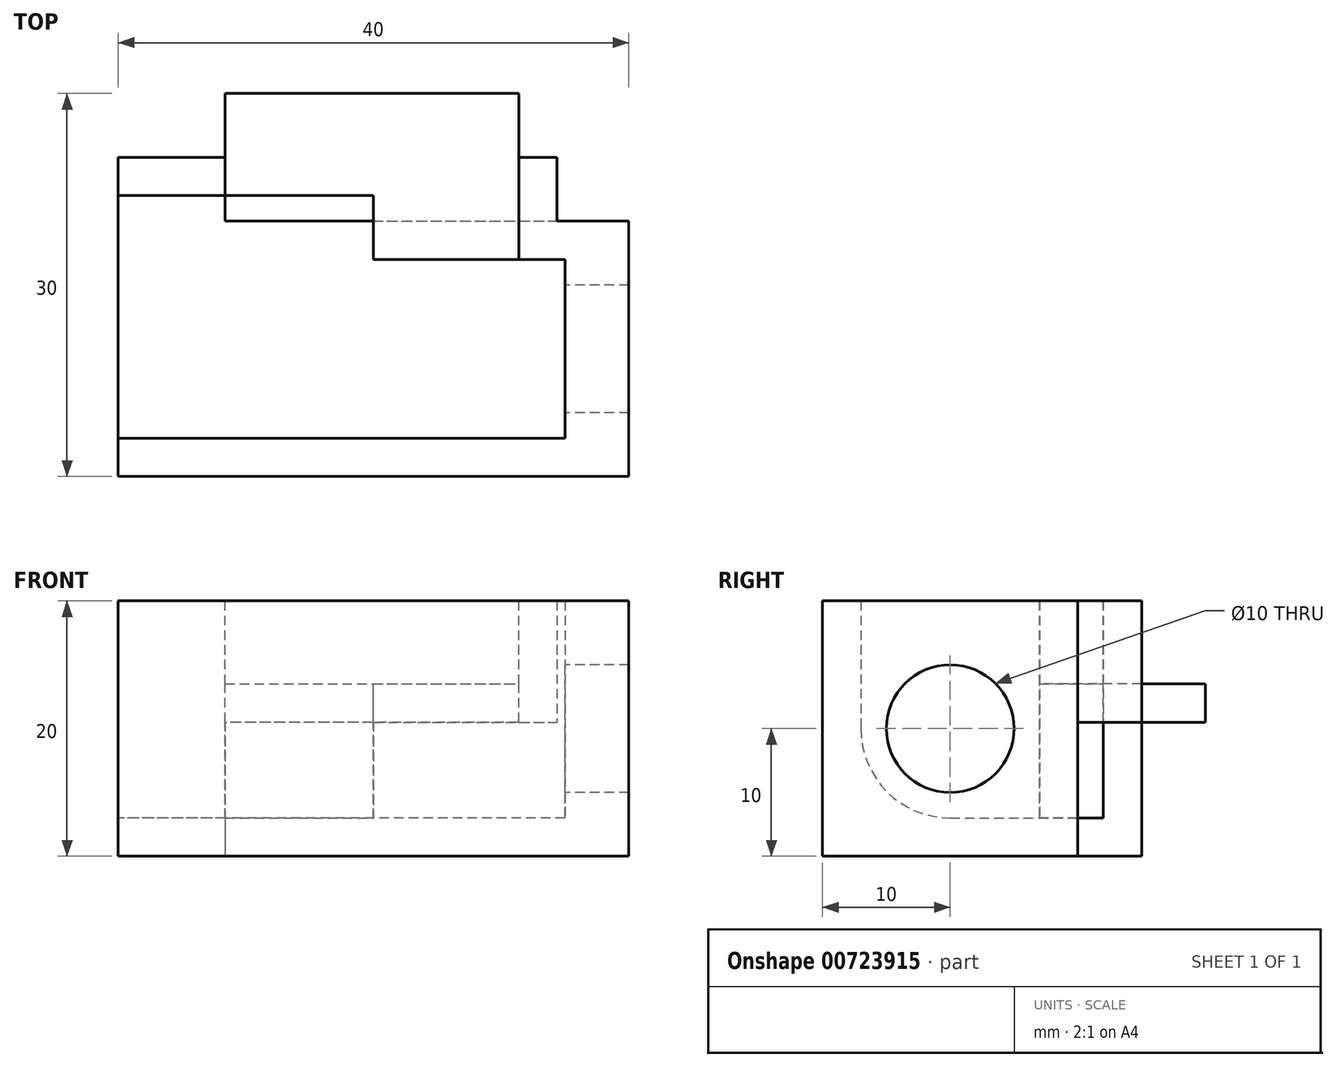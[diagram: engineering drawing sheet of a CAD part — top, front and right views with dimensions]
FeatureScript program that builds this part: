
annotation { "Feature Type Name" : "Feature", "Feature Type Description" : "" }
export const myFeature = defineFeature(function(context is Context, id is Id, definition is map)
    precondition{}
    {
        {
            var Q0;
            Q0=qCreatedBy(makeId("Top.planeOp"),FACE);
            var sketch = newSketch(context, id + "F0", { "sketchPlane" : qUnion([Q0])});
            skLineSegment(sketch, "E0.bottom", {"start": v(-20, 10) * mm, "end": v(20, 10) * mm});
            skLineSegment(sketch, "E0.top", {"start": v(-20, -10) * mm, "end": v(20, -10) * mm});
            skLineSegment(sketch, "E0.left", {"start": v(-20, 10) * mm, "end": v(-20, -10) * mm});
            skLineSegment(sketch, "E0.right", {"start": v(20, 10) * mm, "end": v(20, -10) * mm});
            skPoint(sketch, "E0.middle", {"position": v(0, 0) * mm});
            skSolve(sketch);
        }
        {
            var Q0;
            Q0 = qSketchRegion(id + "F0", true);
            extrude(context, id + "F1", {"entities" : qUnion([Q0]), "depth" : 10 * mm, "offsetDistance" : 25 * mm});
        }
        {
            var Q0;
            Q0=makeQuery(id+"F1.opExtrude","SWEPT_FACE",FACE,{"disambiguationData":[OSD([sQuery(id+"F0.wireOp",EDGE,"E0.left")])]});
            var sketch = newSketch(context, id + "F2", { "sketchPlane" : qUnion([Q0])});
            skLineSegment(sketch, "E1", {"start": v(0, 10) * mm, "end": v(0, 3) * mm, "construction": true});
            skCircle(sketch, "E2", {"center": v(0, 10) * mm, "radius": 7 * mm});
            skCircle(sketch, "E3", {"center": v(0, 10) * mm, "radius": 5 * mm});
            skLineSegment(sketch, "E4.bottom", {"start": v(0, 10) * mm, "end": v(-7, 10) * mm});
            skLineSegment(sketch, "E4.top", {"start": v(0, 3) * mm, "end": v(-7, 3) * mm});
            skLineSegment(sketch, "E4.left", {"start": v(0, 10) * mm, "end": v(0, 3) * mm});
            skLineSegment(sketch, "E4.right", {"start": v(-7, 10) * mm, "end": v(-7, 3) * mm});
            skSolve(sketch);
        }
        {
            var Q0;
            Q0=makeQuery(id+"F1.opExtrude","CAP_FACE",FACE,{"disambiguationData":[OSD([sQuery(id+"F0.wireOp",EDGE,"E0.bottom"),sQuery(id+"F0.wireOp",EDGE,"E0.top"),sQuery(id+"F0.wireOp",EDGE,"E0.left"),sQuery(id+"F0.wireOp",EDGE,"E0.right")])],"isStart":false});
            var sketch = newSketch(context, id + "F3", { "sketchPlane" : qUnion([Q0])});
            skLineSegment(sketch, "E5.bottom", {"start": v(20, 10) * mm, "end": v(15, 10) * mm});
            skLineSegment(sketch, "E5.top", {"start": v(20, -10) * mm, "end": v(15, -10) * mm});
            skLineSegment(sketch, "E5.left", {"start": v(20, 10) * mm, "end": v(20, -10) * mm});
            skLineSegment(sketch, "E5.right", {"start": v(15, 10) * mm, "end": v(15, -10) * mm});
            skLineSegment(sketch, "E6.bottom", {"start": v(-20, 10) * mm, "end": v(15, 10) * mm});
            skLineSegment(sketch, "E6.top", {"start": v(-20, 7) * mm, "end": v(15, 7) * mm});
            skLineSegment(sketch, "E6.left", {"start": v(-20, 10) * mm, "end": v(-20, 7) * mm});
            skLineSegment(sketch, "E6.right", {"start": v(15, 10) * mm, "end": v(15, 7) * mm});
            skLineSegment(sketch, "E7.bottom", {"start": v(-20, -10) * mm, "end": v(15, -10) * mm});
            skLineSegment(sketch, "E7.top", {"start": v(-20, -7) * mm, "end": v(15, -7) * mm});
            skLineSegment(sketch, "E7.left", {"start": v(-20, -10) * mm, "end": v(-20, -7) * mm});
            skLineSegment(sketch, "E7.right", {"start": v(15, -10) * mm, "end": v(15, -7) * mm});
            skSolve(sketch);
        }
        {
            var Q0;
            Q0 = qSketchRegion(id + "F3", true);
            extrude(context, id + "F4", {"entities" : qUnion([Q0]), "operationType" : NewBodyOperationType.ADD, "depth" : 10 * mm, "offsetDistance" : 25 * mm});
        }
        {
            var Q0;
            Q0=makeQuery(id+"F4.opExtrude","CAP_FACE",FACE,{"disambiguationData":[OSD([sQuery(id+"F3.wireOp",EDGE,"E5.bottom"),sQuery(id+"F3.wireOp",EDGE,"E5.top"),sQuery(id+"F3.wireOp",EDGE,"E5.left"),sQuery(id+"F3.wireOp",EDGE,"E5.right"),sQuery(id+"F3.wireOp",EDGE,"E6.bottom"),sQuery(id+"F3.wireOp",EDGE,"E6.top"),sQuery(id+"F3.wireOp",EDGE,"E6.left"),sQuery(id+"F3.wireOp",EDGE,"E7.bottom"),sQuery(id+"F3.wireOp",EDGE,"E7.top"),sQuery(id+"F3.wireOp",EDGE,"E7.left")])],"isStart":false});
            var sketch = newSketch(context, id + "F5", { "sketchPlane" : qUnion([Q0])});
            skLineSegment(sketch, "E8.bottom", {"start": v(11.37, 10) * mm, "end": v(-11.63, 10) * mm});
            skLineSegment(sketch, "E8.top", {"start": v(11.37, 7) * mm, "end": v(-11.63, 7) * mm});
            skLineSegment(sketch, "E8.left", {"start": v(11.37, 10) * mm, "end": v(11.37, 7) * mm});
            skLineSegment(sketch, "E8.right", {"start": v(-11.63, 10) * mm, "end": v(-11.63, 7) * mm});
            skSolve(sketch);
        }
        {
            var Q0;
            Q0=makeQuery(id+"F5.imprint","IMPRINT",FACE,{"disambiguationData":[TD([[makeQuery(id+"F5.imprint","IMPRINT",EDGE,{"derivedFrom":sQuery(id+"F5.wireOp",EDGE,"E8.bottom")}),-1.0]])]});
            extrude(context, id + "F6", {"entities" : qUnion([Q0]), "operationType" : NewBodyOperationType.REMOVE, "oppositeDirection" : true, "depth" : 6.5 * mm, "offsetDistance" : 25 * mm});
        }
        {
            var Q0;
            Q0=makeQuery(id+"F4.boolean.opBoolean","MERGE",FACE,{"derivedFrom":[makeQuery(id+"F1.opExtrude","SWEPT_FACE",FACE,{"disambiguationData":[OSD([sQuery(id+"F0.wireOp",EDGE,"E0.bottom")])]}),makeQuery(id+"F4.opExtrude","SWEPT_FACE",FACE,{"disambiguationData":[OSD([sQuery(id+"F3.wireOp",EDGE,"E5.bottom"),sQuery(id+"F3.wireOp",EDGE,"E6.bottom")])]})]});
            var sketch = newSketch(context, id + "F7", { "sketchPlane" : qUnion([Q0])});
            skLineSegment(sketch, "E9.bottom", {"start": v(-11.37, 13.5) * mm, "end": v(11.63, 13.5) * mm});
            skLineSegment(sketch, "E9.top", {"start": v(-11.37, 10.5) * mm, "end": v(11.63, 10.5) * mm});
            skLineSegment(sketch, "E9.left", {"start": v(-11.37, 13.5) * mm, "end": v(-11.37, 10.5) * mm});
            skLineSegment(sketch, "E9.right", {"start": v(11.63, 13.5) * mm, "end": v(11.63, 10.5) * mm});
            skLineSegment(sketch, "E10.bottom", {"start": v(-11.37, 20) * mm, "end": v(-14.37, 20) * mm});
            skLineSegment(sketch, "E10.top", {"start": v(-11.37, 10.5) * mm, "end": v(-14.37, 10.5) * mm});
            skLineSegment(sketch, "E10.left", {"start": v(-11.37, 20) * mm, "end": v(-11.37, 10.5) * mm});
            skLineSegment(sketch, "E10.right", {"start": v(-14.37, 20) * mm, "end": v(-14.37, 10.5) * mm});
            skLineSegment(sketch, "E11.bottom", {"start": v(20, 20) * mm, "end": v(11.63, 20) * mm});
            skLineSegment(sketch, "E11.top", {"start": v(20, 0) * mm, "end": v(11.63, 0) * mm});
            skLineSegment(sketch, "E11.left", {"start": v(20, 20) * mm, "end": v(20, 0) * mm});
            skLineSegment(sketch, "E11.right", {"start": v(11.63, 20) * mm, "end": v(11.63, 0) * mm});
            skSolve(sketch);
        }
        {
            var Q0;
            Q0 = qSketchRegion(id + "F7", true);
            extrude(context, id + "F8", {"entities" : qUnion([Q0]), "operationType" : NewBodyOperationType.ADD, "depth" : 5 * mm, "offsetDistance" : 25 * mm});
        }
        {
            var Q0;
            {var subQ0=sQuery(id+"F7.wireOp",EDGE,"E9.bottom");Q0=makeQuery(id+"F7.imprint","IMPRINT",FACE,{"disambiguationData":[TD([[makeQuery(id+"F7.imprint","IMPRINT",EDGE,{"derivedFrom":subQ0}),1.0]])]});}
            extrude(context, id + "F9", {"entities" : qUnion([Q0]), "operationType" : NewBodyOperationType.ADD, "depth" : 10 * mm, "offsetDistance" : 25 * mm});
        }
        {
            var Q0;
            {var subQ0=sQuery(id+"F2.wireOp",EDGE,"E2");var subQ1=makeQuery(id+"F1.opExtrude","CAP_EDGE",EDGE,{"disambiguationData":[OSD([sQuery(id+"F0.wireOp",EDGE,"E0.left")])],"isStart":false});var subQ2=makeQuery(id+"F2.imprint","INTERSECT",VERTEX,{"disambiguationData":[OD(0.0)],"derivedFrom":[subQ1,subQ0]});Q0=makeQuery(id+"F2.imprint","IMPRINT",FACE,{"disambiguationData":[TD([[makeQuery(id+"F2.imprint","IMPRINT",EDGE,{"disambiguationData":[TD([[subQ2,-1.0]])],"derivedFrom":subQ0}),1.0]])]});}
            extrude(context, id + "F10", {"entities" : qUnion([Q0]), "operationType" : NewBodyOperationType.REMOVE, "oppositeDirection" : true, "depth" : 35 * mm, "offsetDistance" : 25 * mm});
        }
        {
            var Q0;
            {var subQ0=sQuery(id+"F2.wireOp",EDGE,"E3");var subQ1=makeQuery(id+"F1.opExtrude","CAP_EDGE",EDGE,{"disambiguationData":[OSD([sQuery(id+"F0.wireOp",EDGE,"E0.left")])],"isStart":false});var subQ2=makeQuery(id+"F2.imprint","INTERSECT",VERTEX,{"disambiguationData":[OD(0.0)],"derivedFrom":[subQ1,subQ0]});Q0=makeQuery(id+"F2.imprint","IMPRINT",FACE,{"disambiguationData":[TD([[makeQuery(id+"F2.imprint","IMPRINT",EDGE,{"disambiguationData":[TD([[subQ2,-1.0]])],"derivedFrom":subQ0}),1.0]])]});}
            var Q1;
            {var subQ0=sQuery(id+"F2.wireOp",EDGE,"E3");var subQ1=makeQuery(id+"F1.opExtrude","CAP_EDGE",EDGE,{"disambiguationData":[OSD([sQuery(id+"F0.wireOp",EDGE,"E0.left")])],"isStart":false});var subQ2=makeQuery(id+"F2.imprint","INTERSECT",VERTEX,{"disambiguationData":[OD(0.0)],"derivedFrom":[subQ1,subQ0]});Q1=makeQuery(id+"F2.imprint","IMPRINT",FACE,{"disambiguationData":[TD([[makeQuery(id+"F2.imprint","IMPRINT",EDGE,{"disambiguationData":[TD([[subQ2,1.0]])],"derivedFrom":subQ0}),1.0]])]});}
            extrude(context, id + "F11", {"entities" : qUnion([Q0, Q1]), "operationType" : NewBodyOperationType.REMOVE, "oppositeDirection" : true, "depth" : 40 * mm, "offsetDistance" : 25 * mm});
        }
        {
            var Q0;
            {var subQ0=sQuery(id+"F2.wireOp",EDGE,"E4.bottom");var subQ1=sQuery(id+"F2.wireOp",EDGE,"E3");var subQ2=makeQuery(id+"F2.imprint","INTERSECT",VERTEX,{"derivedFrom":[subQ1,subQ0]});Q0=makeQuery(id+"F2.imprint","IMPRINT",FACE,{"disambiguationData":[TD([[makeQuery(id+"F2.imprint","IMPRINT",EDGE,{"disambiguationData":[TD([[subQ2,-1.0]])],"derivedFrom":subQ1}),1.0]])]});}
            var Q1;
            {var subQ0=sQuery(id+"F2.wireOp",EDGE,"E4.bottom");var subQ5=sQuery(id+"F2.wireOp",EDGE,"E3");var subQ6=makeQuery(id+"F2.imprint","INTERSECT",VERTEX,{"derivedFrom":[subQ5,subQ0]});Q1=makeQuery(id+"F2.imprint","IMPRINT",FACE,{"disambiguationData":[TD([[makeQuery(id+"F2.imprint","IMPRINT",EDGE,{"disambiguationData":[TD([[subQ6,-1.0]])],"derivedFrom":subQ5}),-1.0]])]});}
            var Q2;
            {var subQ2=sQuery(id+"F2.wireOp",EDGE,"E4.top");Q2=makeQuery(id+"F2.imprint","IMPRINT",FACE,{"disambiguationData":[TD([[makeQuery(id+"F2.imprint","IMPRINT",EDGE,{"derivedFrom":subQ2}),-1.0]])]});}
            extrude(context, id + "F12", {"entities" : qUnion([Q0, Q1, Q2]), "operationType" : NewBodyOperationType.REMOVE, "oppositeDirection" : true, "depth" : 35 * mm, "offsetDistance" : 25 * mm});
        }
        {
            var Q0;
            {var subQ0=sQuery(id+"F2.wireOp",EDGE,"E4.bottom");var subQ1=sQuery(id+"F2.wireOp",EDGE,"E3");var subQ2=makeQuery(id+"F2.imprint","INTERSECT",VERTEX,{"derivedFrom":[subQ1,subQ0]});Q0=makeQuery(id+"F2.imprint","IMPRINT",FACE,{"disambiguationData":[TD([[makeQuery(id+"F2.imprint","IMPRINT",EDGE,{"disambiguationData":[TD([[subQ2,-1.0]])],"derivedFrom":subQ1}),1.0]])]});}
            extrude(context, id + "F13", {"entities" : qUnion([Q0]), "operationType" : NewBodyOperationType.REMOVE, "oppositeDirection" : true, "depth" : 40 * mm, "offsetDistance" : 25 * mm});
        }
        {
            var Q0;
            {var subQ0=sQuery(id+"F2.wireOp",EDGE,"E4.left");var subQ5=sQuery(id+"F2.wireOp",EDGE,"E3");var subQ6=makeQuery(id+"F2.imprint","INTERSECT",VERTEX,{"derivedFrom":[subQ5,subQ0]});Q0=makeQuery(id+"F2.imprint","IMPRINT",FACE,{"disambiguationData":[TD([[makeQuery(id+"F2.imprint","IMPRINT",EDGE,{"disambiguationData":[TD([[subQ6,-1.0]])],"derivedFrom":subQ5}),-1.0]])]});}
            extrude(context, id + "F14", {"entities" : qUnion([Q0]), "operationType" : NewBodyOperationType.REMOVE, "oppositeDirection" : true, "depth" : 35 * mm, "offsetDistance" : 25 * mm});
        }
        {
            var Q0;
            Q0=makeQuery(id+"F12.boolean.opBoolean","MERGE",FACE,{"derivedFrom":[makeQuery(id+"F4.opExtrude","SWEPT_FACE",FACE,{"disambiguationData":[OSD([sQuery(id+"F3.wireOp",EDGE,"E6.top")])]}),makeQuery(id+"F12.opExtrude","SWEPT_FACE",FACE,{"disambiguationData":[OSD([sQuery(id+"F2.wireOp",EDGE,"E4.right")])]})]});
            var sketch = newSketch(context, id + "F15", { "sketchPlane" : qUnion([Q0])});
            skPoint(sketch, "E12.oppositeSnap0", {"position": v(-15.81, 20) * mm});
            skLineSegment(sketch, "E12.bottom", {"start": v(-20, 3) * mm, "end": v(0, 3) * mm});
            skLineSegment(sketch, "E12.top", {"start": v(-20, 20) * mm, "end": v(0, 20) * mm});
            skLineSegment(sketch, "E12.left", {"start": v(-20, 3) * mm, "end": v(-20, 20) * mm});
            skLineSegment(sketch, "E12.right", {"start": v(0, 3) * mm, "end": v(0, 20) * mm});
            skSolve(sketch);
        }
        {
            var Q0;
            Q0 = qSketchRegion(id + "F15", true);
            extrude(context, id + "F16", {"entities" : qUnion([Q0]), "operationType" : NewBodyOperationType.REMOVE, "oppositeDirection" : true, "depth" : 5 * mm, "offsetDistance" : 25 * mm});
        }
    });
